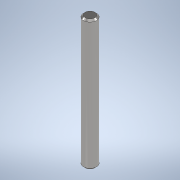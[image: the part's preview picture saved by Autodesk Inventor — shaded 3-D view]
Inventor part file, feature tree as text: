
AUTODESK INVENTOR PART (.ipt)
format: ipt  version: 2021 (Build 250183000, 183)  size: 96,256 bytes
history: native  units: mm
features: extrude x1, chamfer x1, sketch x1
ambient origin geometry x8: Origin, YZ Plane, XZ Plane, XY Plane, X Axis, Y Axis, Z Axis, Center Point
bodies: Solid1 (feature_tree)
feature tree (3):
  extrude  "Extrusion1"  Depth=80.5mm TaperAngle=0.0deg
  chamfer  "Chamfer1"  Distance=1.0mm Angle=45.0deg
  sketch  "Sketch1"  dims[d0=8.0mm d1=80.5mm d2=0.0mm d3=1.0mm d4=2.0mm d5=45.0deg]
